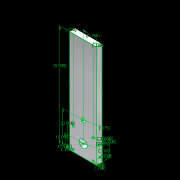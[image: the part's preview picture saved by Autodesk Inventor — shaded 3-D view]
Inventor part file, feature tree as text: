
AUTODESK INVENTOR PART (.ipt)
format: ipt  version: 2012 (Build 160160000, 160)  size: 134,144 bytes
history: native  units: in
note: dims shown in document units (in); Inventor stores cm internally (conversion verified against a paired STEP export)
features: hole x8, other x3, sketch x2, extrude x1
ambient origin geometry x8: Origin, YZ Plane, XZ Plane, XY Plane, X Axis, Y Axis, Z Axis, Center Point
bodies: Solid1 (feature_tree)
feature tree (14):
  extrude  "Extrusion1"  Depth=9.5in
  hole  "Hole15"  [1 undecoded]
  hole  "Hole16"  [1 undecoded]
  hole  "Hole17"  [1 undecoded]
  hole  "Hole18"  [1 undecoded]
  hole  "Hole19"  [1 undecoded]
  hole  "Hole20"  [1 undecoded]
  other  "Font"
  other  "bottom"
  other  "Right"
  hole  "Hole25"  [1 undecoded]
  hole  "Hole26"  [1 undecoded]
  sketch  "Sketch6"  dims[d2=0.5in d3=0.0in d130=0.32in d131=0.195in d132=0.2in d133=0.75in d134=0.375in d135=0.25in d136=0.5635in d137=0.5in d138=0.8108in d139=0.32in d140=0.195in d141=0.2in d142=0.75in d143=0.375in d144=0.25in d145=0.5635in d146=0.5in d147=0.8108in d148=0.32in d149=2.055in d150=0.2in d151=0.75in d152=0.375in d153=0.25in d154=0.5635in d155=0.5in d156=0.8108in d157=0.32in d158=2.055in d159=0.2in d160=0.75in d161=0.375in d162=0.25in d163=0.5635in d164=0.5in d165=0.8108in d166=3.0in d167=1.25in d168=0.375in d169=0.75in d170=0.375in d171=0.25in d172=0.5635in d173=0.5in d174=0.8108in d175=1.25in d176=1.125in d177=0.75in d178=0.75in d179=0.375in d180=0.25in d181=0.5635in d182=0.5in d183=0.8108in d220=9.5in d221=0.2in d222=0.375in d223=0.75in d224=0.32in d225=0.195in d226=1.125in d227=3.0in d228=0.32in d229=0.195in d230=2.055in d231=2.055in d233=0.5in d238=1.25in d239=0.25in d240=0.5in d241=0.19in d242=0.75in d243=0.375in d244=0.25in d245=0.5635in d246=0.75in d247=0.8108in d248=0.25in d249=1.5in d250=0.19in d251=0.75in d252=0.375in d253=0.25in d254=0.5635in d255=0.75in d256=0.8108in d257=0.19in d260=1.5in d261=0.5in d13=1.0in d14=1.0in d40=1.0in d41=1.0in]
  sketch  "Sketch1"  dims[d0=2.5in d1=9.5in]
note: 8 required parameter values undecoded (feature->parameter linkage not recoverable at this tier; creation-order binding heuristic only, values carry confidence <= 0.55)
